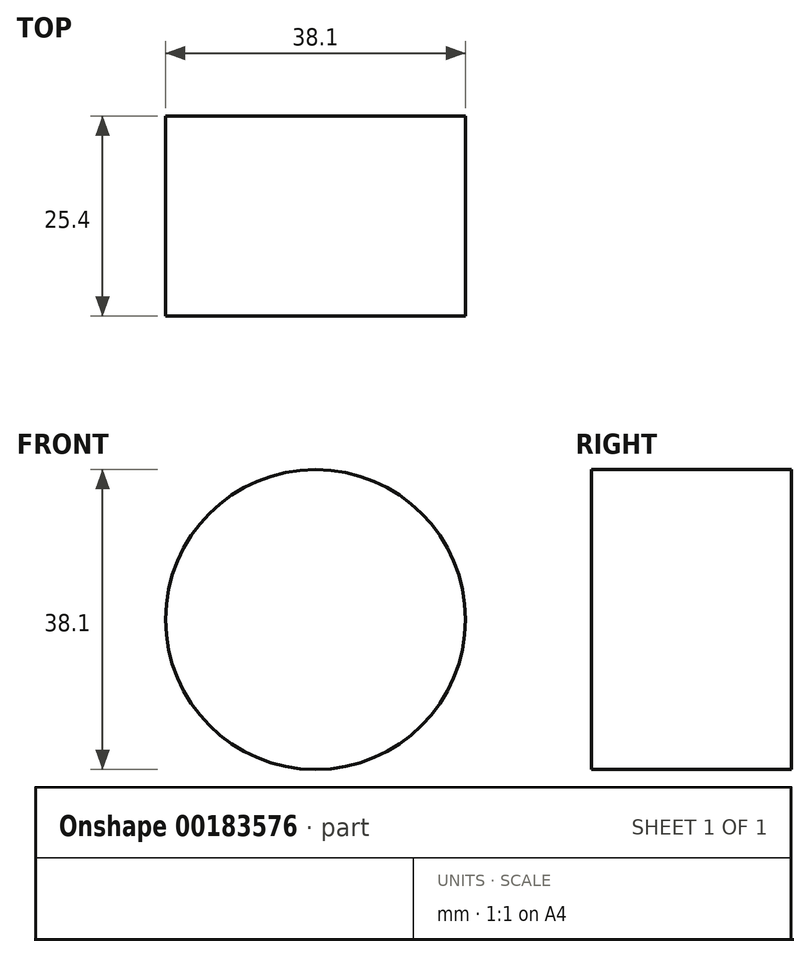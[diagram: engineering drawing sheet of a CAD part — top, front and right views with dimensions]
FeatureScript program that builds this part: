
annotation { "Feature Type Name" : "Feature", "Feature Type Description" : "" }
export const myFeature = defineFeature(function(context is Context, id is Id, definition is map)
    precondition{}
    {
        {
            var Q0;
            Q0=qCreatedBy(makeId("Front.planeOp"),FACE);
            var sketch = newSketch(context, id + "F0", { "sketchPlane" : qUnion([Q0])});
            skCircle(sketch, "E0", {"center": v(0, 0) * mm, "radius": 19.05 * mm});
            skSolve(sketch);
        }
        {
            var Q0;
            Q0 = qSketchRegion(id + "F0", true);
            extrude(context, id + "F1", {"entities" : qUnion([Q0]), "depth" : 25.4 * mm});
        }
    });
